# Revit family: Shower-Valve_Trim-KOHLER-Taut-K-T74041BR
name_source: partatom
category: Specialty Equipment
units: mm (PartAtom-declared; Revit-internal decimal feet)

## family parameters
Cut with Voids When Loaded = No
Host = Face
OmniClass Number = 23.31.25.00
Part Type = Normal
Room Calculation Point = No
Round Connector Dimension = Use Diameter
Shared = No

## types (5) — shared parameters
ADA Compliant = No
Assembly Code = C1030200
Date Modified = 12/10/2024
Default Elevation = 42"
Description = Finishing for Single-Lever Mixer With Bathtub / Shower Diverter
Handle Clearance = 3 1/16"
Height = 6 9/16"
Length = 2 13/16"
Manufacturer = Kohler Co
Master Format 2014 = 10 28 00
Master Format 2014 Name = Toilet, Bath, and Laundry Accessories
Material = Premium Metal Construction
Product Documentation Link = https://techcomm.kohler.com
Product Name = Taut
URL = https://br.kohler.com
WaterSense Certified = No
Width = 4 7/16"

## per-type parameters (varying)
| type | Finish | Model | Product Page URL | Type |
| CP-Polished Chrome | Kohler-Metal-CP-Polished_Chrome | K-T74041BR-4-CP | https://br.kohler.com | 1 |
| BL-Matte Black | Kohler-Metal-BL-Matte_Black | K-T74041BR-4-BL | https://br.kohler.com | 2 |
| BN-Vibrant Brushed Nickel | Kohler-Metal-BN-Vibrant_Brushed_Nickel | K-T74041BR-4-BN |  | 3 |
| RGD-Polished Rose Gold | Kohler-Metal-RGD-Polished_Rose_Gold | K-T74041BR-4-RGD |  | 4 |
| 2MB-Vibrant Brushed Moderne Brass | Kohler-Metal-2MB-Vibrant_Brushed_Moderne_Brass | K-T74041BR-4-2MB |  | 5 |

## geometry (parser evidence)
native form markers: Sweep x6
no freeform markers — native parametric forms only
